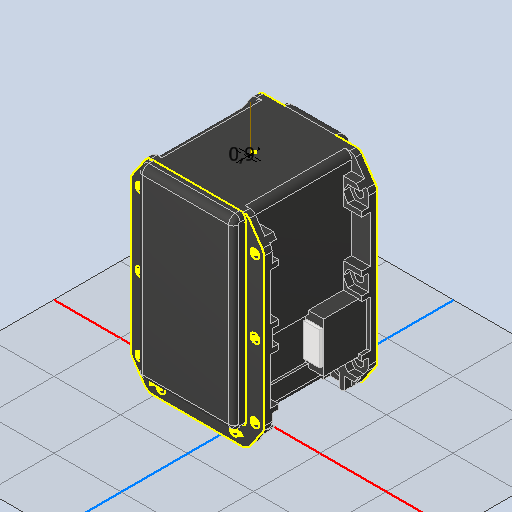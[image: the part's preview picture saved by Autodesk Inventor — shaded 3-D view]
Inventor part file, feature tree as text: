
AUTODESK INVENTOR PART (.ipt)
format: ipt  version: 2022 (Build 260153000, 153)  size: 559,616 bytes
history: native  units: mm
features: sketch x4, projected_geometry x3, extrude x1, other x1, imported_body x1
ambient origin geometry x8: Origin, YZ Plane, XZ Plane, XY Plane, X Axis, Y Axis, Z Axis, Center Point
bodies: Solid1 (feature_tree)
feature tree (10):
  extrude  "Extrusion1"  Depth=10.0mm
  sketch  "Эскиз2"
  sketch  "Эскиз3"
  sketch  "Эскиз4"
  other  "РабОсь1"
  sketch  "Sketch1"  dims[d0=10.0mm d1=0.0mm d2=0.9mm]
  projected_geometry  "Projected Loop1"
  projected_geometry  "Спроецированная петля2"
  projected_geometry  "Спроецированная петля3"
  imported_body  "Base1"
